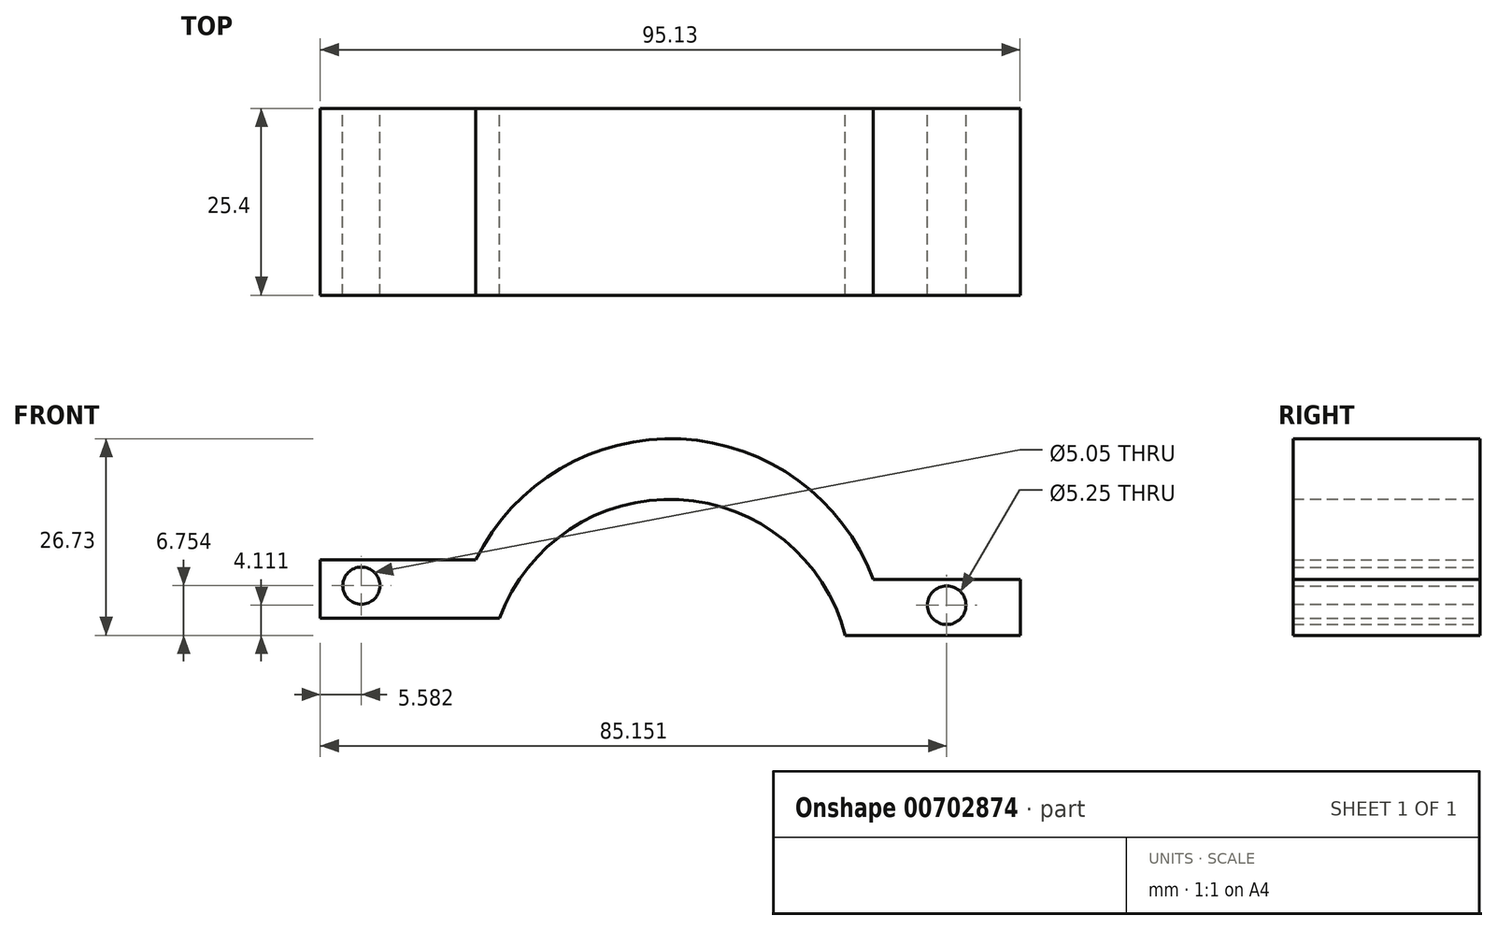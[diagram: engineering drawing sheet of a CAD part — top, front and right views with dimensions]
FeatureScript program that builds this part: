
annotation { "Feature Type Name" : "Feature", "Feature Type Description" : "" }
export const myFeature = defineFeature(function(context is Context, id is Id, definition is map)
    precondition{}
    {
        {
            var Q0;
            Q0=qCreatedBy(makeId("Front.planeOp"),FACE);
            var sketch = newSketch(context, id + "F0", { "sketchPlane" : qUnion([Q0])});
            skLineSegment(sketch, "E0", {"start": v(-48.89, -27.01) * mm, "end": v(-48.89, -34.94) * mm});
            skLineSegment(sketch, "E1", {"start": v(-48.89, -34.94) * mm, "end": v(-24.52, -34.94) * mm});
            skLineSegment(sketch, "E2", {"start": v(-48.89, -27.01) * mm, "end": v(-27.75, -27.01) * mm});
            skLineSegment(sketch, "E3", {"start": v(22.46, -37.29) * mm, "end": v(46.24, -37.29) * mm});
            skLineSegment(sketch, "E4", {"start": v(46.24, -37.29) * mm, "end": v(46.24, -29.66) * mm});
            skLineSegment(sketch, "E5", {"start": v(46.24, -29.66) * mm, "end": v(26.28, -29.66) * mm});
            skArc(sketch, "E6", {"start": v(22.46, -37.29) * mm, "mid": v(-0.16, -18.82) * mm, "end": v(-24.52, -34.94) * mm});
            skArc(sketch, "E7", {"start": v(26.28, -29.66) * mm, "mid": v(0.13, -10.6) * mm, "end": v(-27.75, -27.01) * mm});
            skCircle(sketch, "E8", {"center": v(-43.3, -30.54) * mm, "radius": 2.53 * mm});
            skCircle(sketch, "E9", {"center": v(36.26, -33.18) * mm, "radius": 2.63 * mm});
            skSolve(sketch);
        }
        {
            var Q0;
            Q0 = qSketchRegion(id + "F0", true);
            extrude(context, id + "F1", {"entities" : qUnion([Q0]), "depth" : 25.4 * mm, "offsetDistance" : 25.4 * mm});
        }
    });
